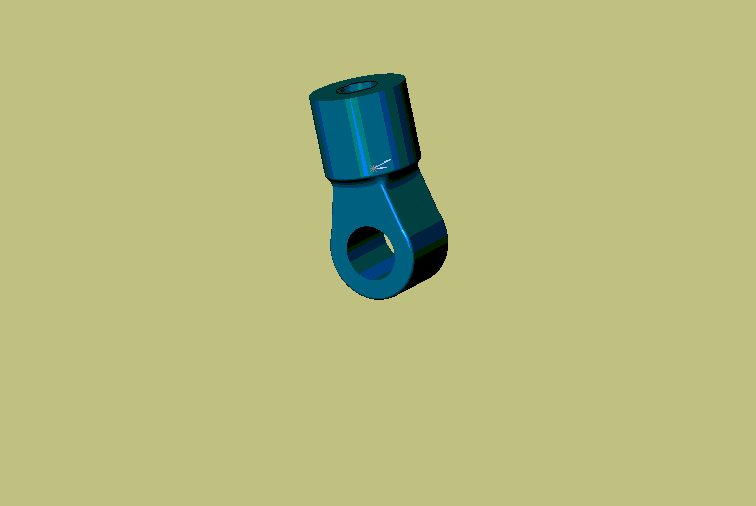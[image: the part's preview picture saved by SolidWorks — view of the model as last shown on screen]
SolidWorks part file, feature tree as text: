
SOLIDWORKS PART (.sldprt)
format: sldprt  version: not decoded by parser v0  size: 291,840 bytes
history: native  units: mm
features: sketch x4, plane x3, extrude x2, fillet x2, material x1, hole x1, thread x1 (+8 scaffold rows collapsed)
feature tree (22):
  scaffold x8  (default folders/planes/origin — collapsed)
  material  "Matériau <non spécifié>"
  plane  "Plane1"
  plane  "Plane2"
  plane  "Plane3"
  sketch  "Esquisse1"  dims[D1=7.0mm]
  extrude  "Base-Extrusion"  Depth=6mm
  sketch  "Esquisse2"  dims[D1=7.0mm D2=4.0mm]
  extrude  "Boss.-Extru.1"  Depth=5mm
  hole  "Perçage1"  Diameter=2.5mm Depth=9mm
  sketch  "Esquisse4"
  sketch  "Esquisse3"  dims[hole-wizard template sketch: 47 standard entries collapsed; hole parameters kept: c15.Profondeur du perçage=9.0mm c15.D3=~14.816244mm c15.Angle de pointe=180.0deg]
  thread  "Représentation de filetage1"  Diameter=8mm  [1 undecoded]
  fillet  "Congé2"  Radius=0.25mm
  fillet  "Congé3"  Radius=1mm
decode coverage: 9 of 10 modeling features carry decoded parameters
note: ~ marks probable driven/reference dimensions
note: 1 parameter value undecoded
note: suppression state not decoded; provenance and decode notes live in map.json
